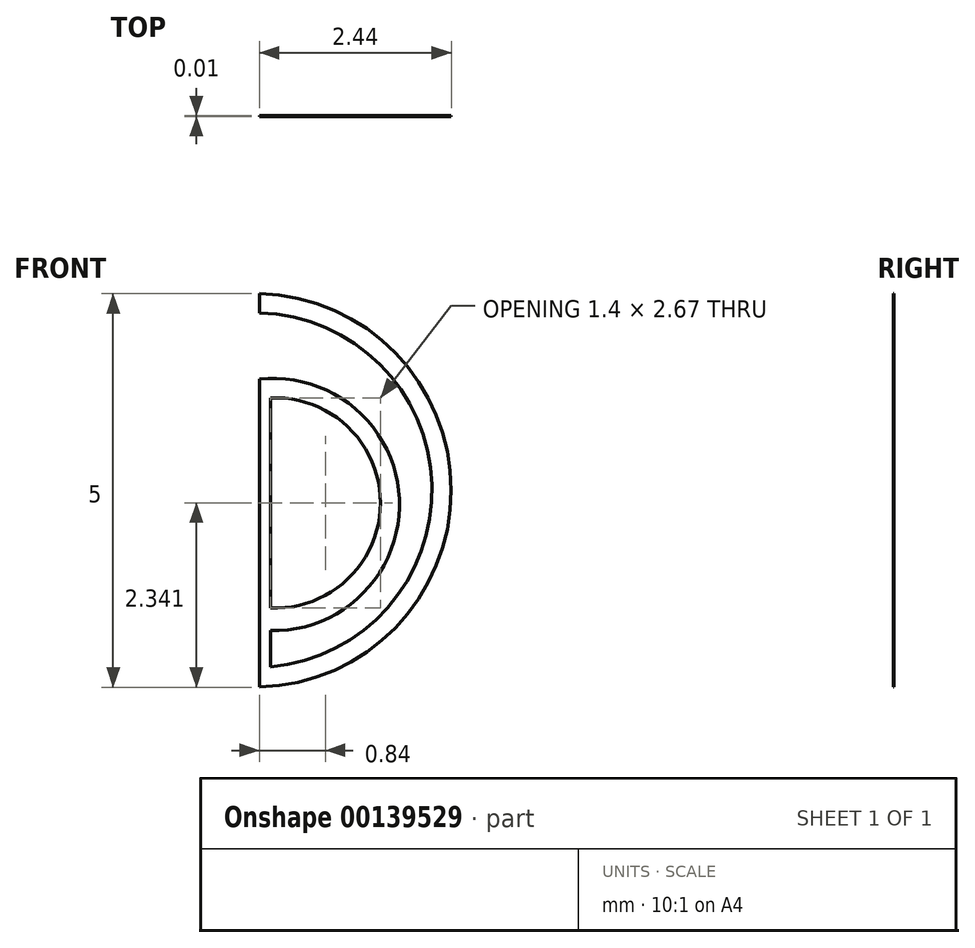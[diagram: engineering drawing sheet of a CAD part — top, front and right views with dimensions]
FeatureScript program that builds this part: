
annotation { "Feature Type Name" : "Feature", "Feature Type Description" : "" }
export const myFeature = defineFeature(function(context is Context, id is Id, definition is map)
    precondition{}
    {
        {
            var Q0;
            Q0=qCreatedBy(makeId("Front.planeOp"),FACE);
            var sketch = newSketch(context, id + "F0", { "sketchPlane" : qUnion([Q0])});
            skArc(sketch, "E0", {"start": v(0, -2.26) * mm, "mid": v(2.2, 0) * mm, "end": v(0, 2.25) * mm});
            skLineSegment(sketch, "E1", {"start": v(0, -2.26) * mm, "end": v(0, 1.15) * mm});
            skArc(sketch, "E2", {"start": v(0, -1.49) * mm, "mid": v(1.54, -0.17) * mm, "end": v(0, 1.15) * mm});
            skLineSegment(sketch, "E3", {"start": v(0, 1.15) * mm, "end": v(0, 1.4) * mm});
            skArc(sketch, "E4", {"start": v(0, -1.78) * mm, "mid": v(1.78, -0.19) * mm, "end": v(0, 1.4) * mm});
            skLineSegment(sketch, "E5", {"start": v(0, 2.25) * mm, "end": v(0, 2.5) * mm});
            skLineSegment(sketch, "E6", {"start": v(0, -2.26) * mm, "end": v(0, -2.5) * mm});
            skArc(sketch, "E7", {"start": v(0, -2.5) * mm, "mid": v(2.44, 0) * mm, "end": v(0, 2.5) * mm});
            skLineSegment(sketch, "E8", {"start": v(0.14, 1.16) * mm, "end": v(0.14, -2.26) * mm});
            skSolve(sketch);
        }
        {
            var Q0;
            Q0 = qSketchRegion(id + "F0", true);
            extrude(context, id + "F1", {"entities" : qUnion([Q0]), "depth" : 0.01 * mm});
        }
    });
